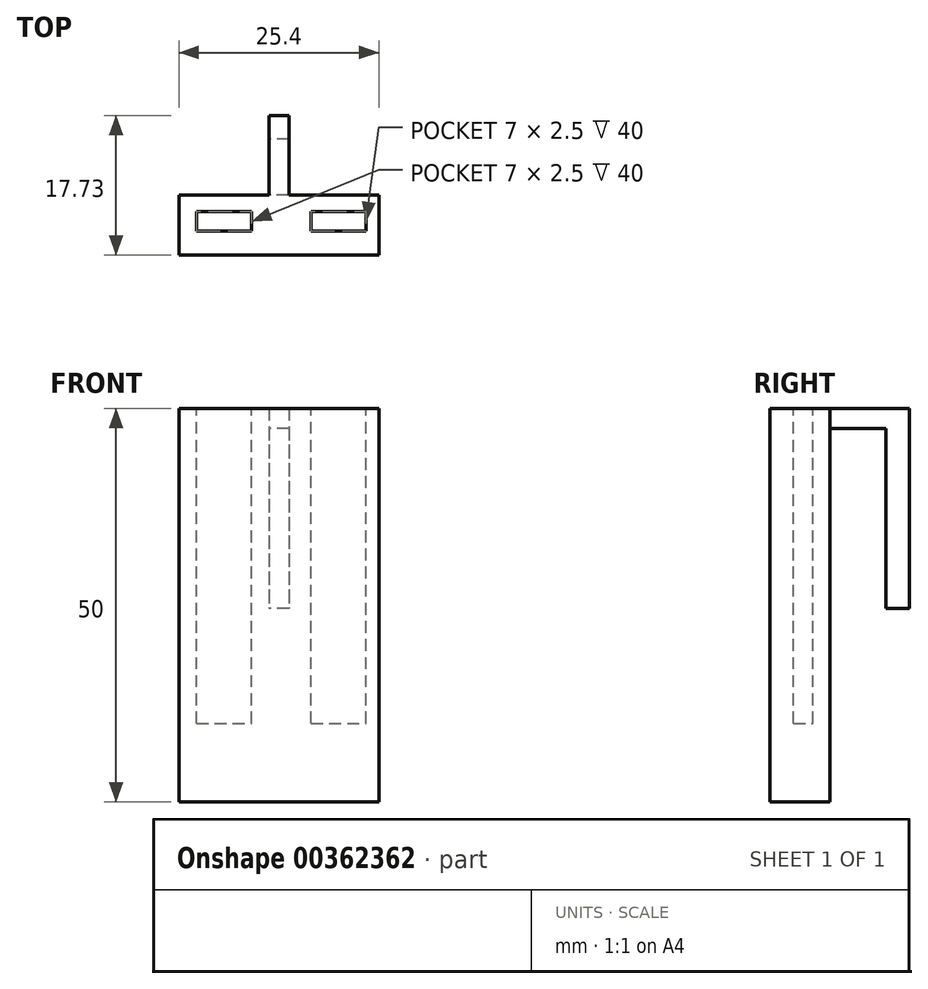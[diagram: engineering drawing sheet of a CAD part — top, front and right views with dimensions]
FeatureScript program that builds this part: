
annotation { "Feature Type Name" : "Feature", "Feature Type Description" : "" }
export const myFeature = defineFeature(function(context is Context, id is Id, definition is map)
    precondition{}
    {
        {
            var Q0;
            Q0=qCreatedBy(makeId("Front.planeOp"),FACE);
            var sketch = newSketch(context, id + "F0", { "sketchPlane" : qUnion([Q0])});
            skLineSegment(sketch, "E0.bottom", {"start": v(12.7, -25) * mm, "end": v(-12.7, -25) * mm});
            skLineSegment(sketch, "E0.top", {"start": v(12.7, 25) * mm, "end": v(-12.7, 25) * mm});
            skLineSegment(sketch, "E0.left", {"start": v(12.7, -25) * mm, "end": v(12.7, 25) * mm});
            skLineSegment(sketch, "E0.right", {"start": v(-12.7, -25) * mm, "end": v(-12.7, 25) * mm});
            skPoint(sketch, "E0.middle", {"position": v(0, 0) * mm});
            skSolve(sketch);
        }
        {
            var Q0;
            Q0 = qSketchRegion(id + "F0", true);
            extrude(context, id + "F1", {"entities" : qUnion([Q0]), "depth" : 7.62 * mm});
        }
        {
            var Q0;
            Q0=qCreatedBy(makeId("Right.planeOp"),FACE);
            var sketch = newSketch(context, id + "F2", { "sketchPlane" : qUnion([Q0])});
            skLineSegment(sketch, "E1.bottom", {"start": v(0, 25) * mm, "end": v(7.11, 25) * mm});
            skLineSegment(sketch, "E1.top", {"start": v(0, 22.46) * mm, "end": v(7.11, 22.46) * mm});
            skLineSegment(sketch, "E1.left", {"start": v(0, 25) * mm, "end": v(0, 22.46) * mm});
            skLineSegment(sketch, "E1.right", {"start": v(7.11, 25) * mm, "end": v(7.11, 22.46) * mm});
            skSolve(sketch);
        }
        {
            var Q0;
            Q0=makeQuery(id+"F2.imprint","IMPRINT",FACE,{"disambiguationData":[TD([[makeQuery(id+"F2.imprint","IMPRINT",EDGE,{"derivedFrom":sQuery(id+"F2.wireOp",EDGE,"E1.bottom")}),-1.0]])]});
            extrude(context, id + "F3", {"entities" : qUnion([Q0]), "operationType" : NewBodyOperationType.ADD, "depth" : 1.27 * mm});
        }
        {
            var Q0;
            Q0=makeQuery(id+"F3.opExtrude","CAP_FACE",FACE,{"disambiguationData":[OSD([sQuery(id+"F2.wireOp",EDGE,"E1.bottom"),sQuery(id+"F2.wireOp",EDGE,"E1.top"),sQuery(id+"F2.wireOp",EDGE,"E1.left"),sQuery(id+"F2.wireOp",EDGE,"E1.right")])],"isStart":true});
            extrude(context, id + "F4", {"entities" : qUnion([Q0]), "operationType" : NewBodyOperationType.ADD, "depth" : 1.27 * mm});
        }
        {
            var Q0;
            Q0=makeQuery(id+"F4.opExtrude","CAP_FACE",FACE,{"disambiguationData":[OSD([sQuery(id+"F2.wireOp",EDGE,"E1.bottom"),sQuery(id+"F2.wireOp",EDGE,"E1.top"),sQuery(id+"F2.wireOp",EDGE,"E1.left"),sQuery(id+"F2.wireOp",EDGE,"E1.right")])],"isStart":false});
            var sketch = newSketch(context, id + "F5", { "sketchPlane" : qUnion([Q0])});
            skLineSegment(sketch, "E2.bottom", {"start": v(-7.11, 25) * mm, "end": v(-10.11, 25) * mm});
            skLineSegment(sketch, "E2.top", {"start": v(-7.11, -0.4) * mm, "end": v(-10.11, -0.4) * mm});
            skLineSegment(sketch, "E2.left", {"start": v(-7.11, 25) * mm, "end": v(-7.11, -0.4) * mm});
            skLineSegment(sketch, "E2.right", {"start": v(-10.11, 25) * mm, "end": v(-10.11, -0.4) * mm});
            skSolve(sketch);
        }
        {
            var Q0;
            {var subQ1=sQuery(id+"F5.wireOp",EDGE,"E2.bottom");Q0=makeQuery(id+"F5.imprint","IMPRINT",FACE,{"disambiguationData":[TD([[makeQuery(id+"F5.imprint","IMPRINT",EDGE,{"derivedFrom":subQ1}),1.0]])]});}
            extrude(context, id + "F6", {"entities" : qUnion([Q0]), "operationType" : NewBodyOperationType.ADD, "oppositeDirection" : true, "depth" : 2.54 * mm});
        }
        {
            var Q0;
            {var subQ0=sQuery(id+"F2.wireOp",EDGE,"E1.bottom");Q0=makeQuery(id+"F6.boolean.opBoolean","MERGE",FACE,{"derivedFrom":[makeQuery(id+"F4.boolean.opBoolean","MERGE",FACE,{"derivedFrom":[makeQuery(id+"F3.boolean.opBoolean","MERGE",FACE,{"derivedFrom":[makeQuery(id+"F1.opExtrude","SWEPT_FACE",FACE,{"disambiguationData":[OSD([sQuery(id+"F0.wireOp",EDGE,"E0.top")])]}),makeQuery(id+"F3.opExtrude","SWEPT_FACE",FACE,{"disambiguationData":[OSD([subQ0])]})]}),makeQuery(id+"F4.opExtrude","SWEPT_FACE",FACE,{"disambiguationData":[OSD([subQ0])]})]}),makeQuery(id+"F6.opExtrude","SWEPT_FACE",FACE,{"disambiguationData":[OSD([sQuery(id+"F5.wireOp",EDGE,"E2.bottom")])]})]});}
            var sketch = newSketch(context, id + "F7", { "sketchPlane" : qUnion([Q0])});
            skLineSegment(sketch, "E3.bottom", {"start": v(-10.46, -4.61) * mm, "end": v(-3.46, -4.61) * mm});
            skLineSegment(sketch, "E3.top", {"start": v(-10.46, -2.11) * mm, "end": v(-3.46, -2.1) * mm});
            skLineSegment(sketch, "E3.left", {"start": v(-10.46, -4.61) * mm, "end": v(-10.46, -2.11) * mm});
            skLineSegment(sketch, "E3.right", {"start": v(-3.46, -4.6) * mm, "end": v(-3.46, -2.1) * mm});
            skLineSegment(sketch, "E4.bottom", {"start": v(4.09, -4.61) * mm, "end": v(11.09, -4.61) * mm});
            skLineSegment(sketch, "E4.top", {"start": v(4.09, -2.11) * mm, "end": v(11.09, -2.11) * mm});
            skLineSegment(sketch, "E4.left", {"start": v(4.09, -4.61) * mm, "end": v(4.09, -2.11) * mm});
            skLineSegment(sketch, "E4.right", {"start": v(11.09, -4.61) * mm, "end": v(11.09, -2.11) * mm});
            skSolve(sketch);
        }
        {
            var Q0;
            Q0=makeQuery(id+"F7.imprint","IMPRINT",FACE,{"disambiguationData":[TD([[makeQuery(id+"F7.imprint","IMPRINT",EDGE,{"derivedFrom":sQuery(id+"F7.wireOp",EDGE,"E3.bottom")}),1.0]])]});
            var Q1;
            Q1=makeQuery(id+"F7.imprint","IMPRINT",FACE,{"disambiguationData":[TD([[makeQuery(id+"F7.imprint","IMPRINT",EDGE,{"derivedFrom":sQuery(id+"F7.wireOp",EDGE,"E4.bottom")}),1.0]])]});
            extrude(context, id + "F8", {"entities" : qUnion([Q0, Q1]), "operationType" : NewBodyOperationType.REMOVE, "oppositeDirection" : true, "depth" : 40 * mm});
        }
    });
